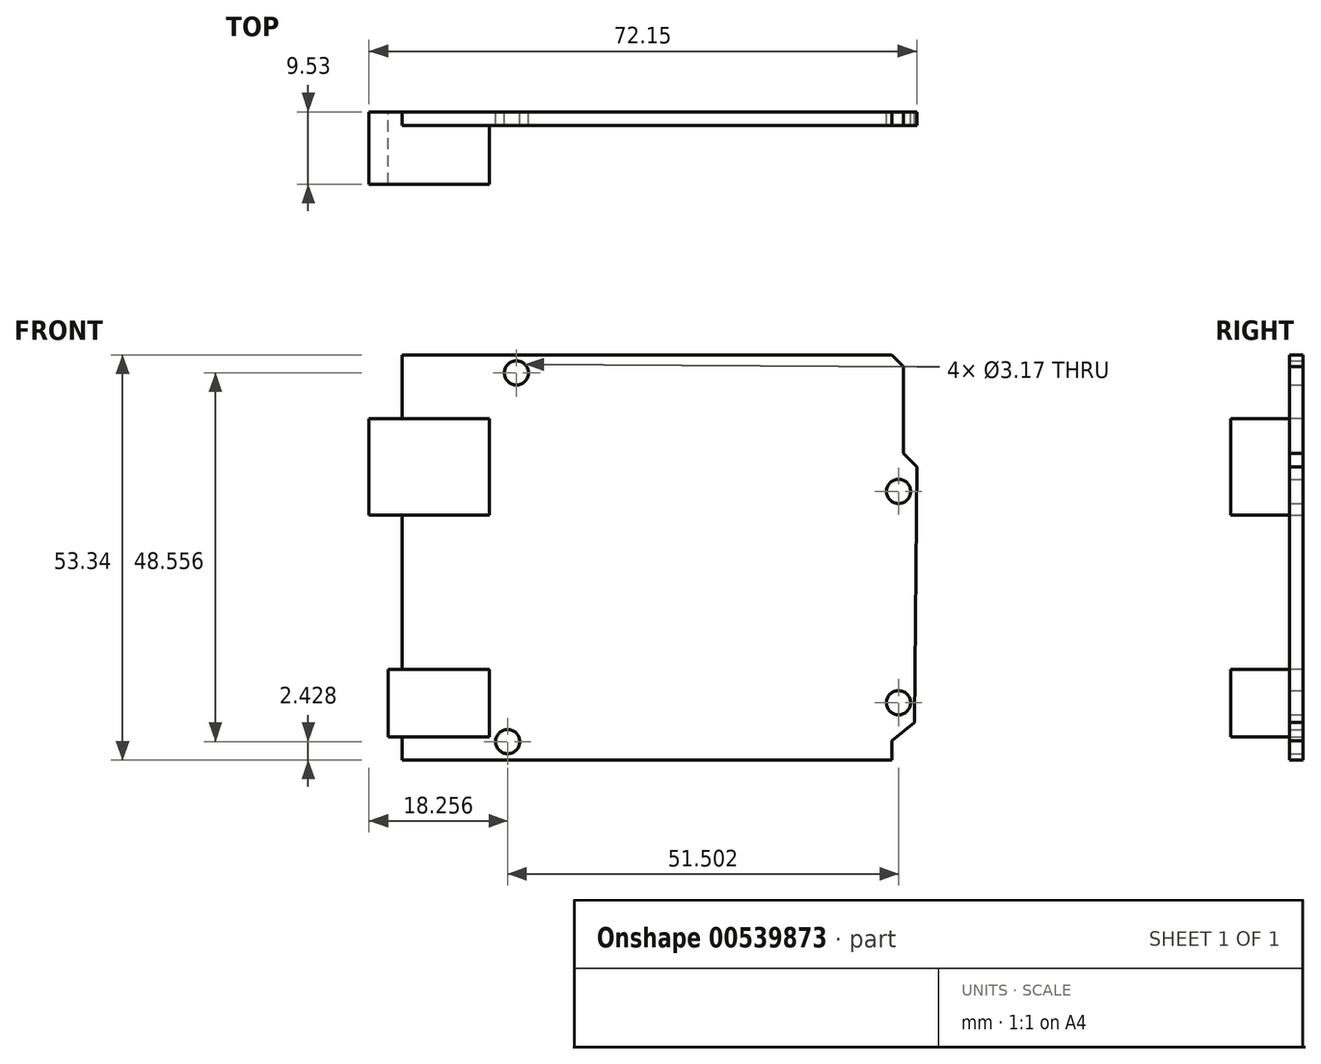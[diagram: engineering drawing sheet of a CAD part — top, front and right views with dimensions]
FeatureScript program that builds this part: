
annotation { "Feature Type Name" : "Feature", "Feature Type Description" : "" }
export const myFeature = defineFeature(function(context is Context, id is Id, definition is map)
    precondition{}
    {
        {
            var Q0;
            Q0=qCreatedBy(makeId("Front.planeOp"),FACE);
            var sketch = newSketch(context, id + "F0", { "sketchPlane" : qUnion([Q0])});
            skLineSegment(sketch, "E0", {"start": v(-35.4, 24.37) * mm, "end": v(-35.4, -28.97) * mm});
            skLineSegment(sketch, "E1", {"start": v(-35.4, 24.37) * mm, "end": v(29.1, 24.37) * mm});
            skLineSegment(sketch, "E2", {"start": v(-35.4, -28.97) * mm, "end": v(29.1, -28.97) * mm});
            skPoint(sketch, "E3.end.orphan", {"position": v(34, -6.43) * mm});
            skPoint(sketch, "E4.orphan", {"position": v(34, -28.97) * mm});
            skLineSegment(sketch, "E5", {"start": v(29.1, -28.97) * mm, "end": v(29.1, -26.43) * mm});
            skLineSegment(sketch, "E6", {"start": v(32.14, -24.02) * mm, "end": v(29.1, -26.43) * mm});
            skPoint(sketch, "E7.end.orphan", {"position": v(32.14, 10.9) * mm});
            skPoint(sketch, "E8.end.orphan", {"position": v(31.14, 10.9) * mm});
            skPoint(sketch, "E9.end.orphan", {"position": v(29.87, 9.64) * mm});
            skLineSegment(sketch, "E10", {"start": v(32.14, -24.02) * mm, "end": v(32.41, 9.64) * mm});
            skLineSegment(sketch, "E11", {"start": v(29.1, 24.37) * mm, "end": v(30.63, 22.85) * mm});
            skPoint(sketch, "E12.orphan", {"position": v(29.87, 12.18) * mm});
            skLineSegment(sketch, "E13", {"start": v(30.63, 22.85) * mm, "end": v(30.63, 11.42) * mm});
            skLineSegment(sketch, "E14", {"start": v(30.63, 11.42) * mm, "end": v(32.41, 9.64) * mm});
            skSolve(sketch);
        }
        {
            var Q0;
            Q0=makeQuery(id+"F0.imprint","IMPRINT",FACE,{"disambiguationData":[TD([[makeQuery(id+"F0.imprint","IMPRINT",EDGE,{"derivedFrom":sQuery(id+"F0.wireOp",EDGE,"E0")}),1.0]])]});
            extrude(context, id + "F1", {"entities" : qUnion([Q0]), "depth" : 1.78 * mm, "offsetDistance" : 25.4 * mm});
        }
        {
            var Q0;
            Q0=qCreatedBy(makeId("Front.planeOp"),FACE);
            var sketch = newSketch(context, id + "F2", { "sketchPlane" : qUnion([Q0])});
            skLineSegment(sketch, "E15", {"start": v(-35.3, -28.97) * mm, "end": v(-23.87, -28.97) * mm});
            skLineSegment(sketch, "E16", {"start": v(-23.87, -28.97) * mm, "end": v(-23.87, -17.04) * mm});
            skPoint(sketch, "E17.start.orphan", {"position": v(-44.12, 3.28) * mm});
            skLineSegment(sketch, "E18", {"start": v(-23.87, 3.28) * mm, "end": v(-39.74, 3.28) * mm});
            skLineSegment(sketch, "E19", {"start": v(-39.74, 3.28) * mm, "end": v(-39.74, 15.98) * mm});
            skLineSegment(sketch, "E20", {"start": v(-23.87, 3.28) * mm, "end": v(-23.87, 15.98) * mm});
            skLineSegment(sketch, "E21", {"start": v(-39.74, 15.98) * mm, "end": v(-23.87, 15.98) * mm});
            skLineSegment(sketch, "E22", {"start": v(-23.87, -25.93) * mm, "end": v(-37.2, -25.93) * mm});
            skLineSegment(sketch, "E23", {"start": v(-37.2, -25.93) * mm, "end": v(-37.2, -17.04) * mm});
            skLineSegment(sketch, "E24", {"start": v(-23.87, -25.93) * mm, "end": v(-23.87, -17.04) * mm});
            skLineSegment(sketch, "E25", {"start": v(-37.2, -17.04) * mm, "end": v(-23.87, -17.04) * mm});
            skSolve(sketch);
        }
        {
            var Q0;
            Q0 = qSketchRegion(id + "F2", true);
            extrude(context, id + "F3", {"entities" : qUnion([Q0]), "operationType" : NewBodyOperationType.ADD, "depth" : 9.52 * mm, "offsetDistance" : 25.4 * mm});
        }
        {
            var Q0;
            Q0=qCreatedBy(makeId("Front.planeOp"),FACE);
            var sketch = newSketch(context, id + "F4", { "sketchPlane" : qUnion([Q0])});
            skPoint(sketch, "E26.end.orphan", {"position": v(-19.13, 22.01) * mm});
            skCircle(sketch, "E27", {"center": v(-20.33, 22.01) * mm, "radius": 1.59 * mm});
            skPoint(sketch, "E28.start.orphan", {"position": v(-20.75, -30.24) * mm});
            skPoint(sketch, "E29.end.orphan", {"position": v(-20.75, -27.7) * mm});
            skPoint(sketch, "E30.orphan", {"position": v(-20.75, -29.42) * mm});
            skCircle(sketch, "E31", {"center": v(-21.48, -26.54) * mm, "radius": 1.59 * mm});
            skPoint(sketch, "E32.orphan", {"position": v(-36.02, 6.41) * mm});
            skCircle(sketch, "E33", {"center": v(30.02, 6.41) * mm, "radius": 1.59 * mm});
            skPoint(sketch, "E34.orphan", {"position": v(24.3, 6.41) * mm});
            skPoint(sketch, "E35.end.orphan", {"position": v(25.93, -21.42) * mm});
            skCircle(sketch, "E36", {"center": v(30, -21.42) * mm, "radius": 1.59 * mm});
            skSolve(sketch);
        }
        {
            var Q0;
            Q0 = qSketchRegion(id + "F4", true);
            extrude(context, id + "F5", {"entities" : qUnion([Q0]), "operationType" : NewBodyOperationType.REMOVE, "depth" : 1.78 * mm, "offsetDistance" : 25.4 * mm});
        }
    });
